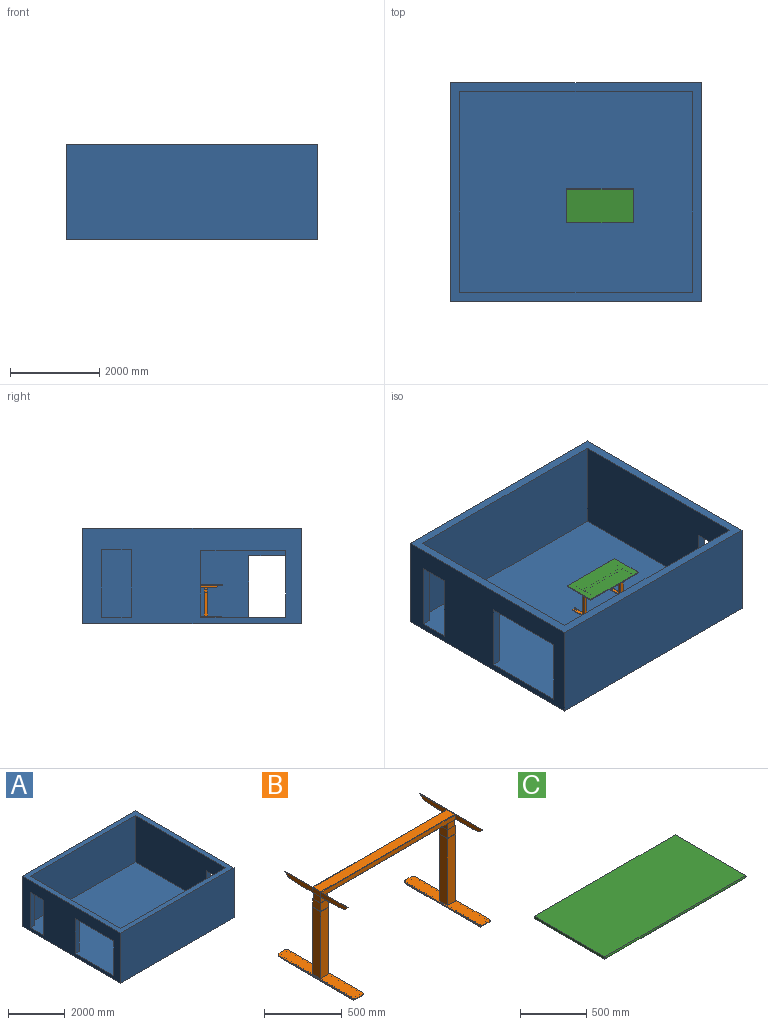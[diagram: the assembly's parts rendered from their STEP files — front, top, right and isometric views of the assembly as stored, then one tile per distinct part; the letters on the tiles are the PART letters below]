
ASSEMBLY  parts=3 mates=2
PART A: 20 faces, bbox 5620x4900x2150 mm
  f0: plane 4500x2000mm, normal (1,0,0), area 5140709mm2, adj f4,f5,f9,f10,f14,f15,f16,f17
  f1: plane 4900x2150mm, normal (-1,0,0), area 6675709mm2, adj f3,f7,f8,f9,f10,f14,f15,f16
  f2: plane 4900x2150mm, normal (1,0,0), area 9320170mm2, adj f3,f7,f8,f9,f10,f11,f12,f13
  f3: plane 5620x4900mm, normal (0,0,-1), area 27538000mm2, adj f1,f2,f7,f8
  f4: plane 5220x2000mm, normal (0,-1,0), area 10440000mm2, adj f0,f6,f9,f10
  f5: plane 5220x2000mm, normal (0,1,0), area 10440000mm2, adj f0,f6,f9,f10
  f6: plane 4500x2000mm, normal (-1,0,0), area 7785170mm2, adj f4,f5,f9,f10,f11,f12,f13
  f7: plane 5620x2150mm, normal (0,1,0), area 12083000mm2, adj f1,f2,f3,f9
  f8: plane 5620x2150mm, normal (0,-1,0), area 12083000mm2, adj f1,f2,f3,f9
  f9: plane 5620x4900mm, normal (0,0,1), area 4048000mm2, adj f0,f1,f2,f4,f5,f6,f7,f8
  f10: plane 5620x4500mm, normal (0,0,1), area 24180418.5mm2, adj f0,f1,f2,f4,f5,f6,f12,f13
  f11: plane 881.69x200mm, normal (0,0,-1), area 176338.6mm2, adj f2,f6,f12,f13
  f12: plane 1377.84x200mm, normal (0,1,0), area 275567.5mm2, adj f2,f6,f10,f11
  f13: plane 1377.84x200mm, normal (0,-1,0), area 275567.5mm2, adj f2,f6,f10,f11
  f14: plane 1496.51x200mm, normal (0,1,0), area 299302.3mm2, adj f0,f1,f10,f15
  f15: plane 1903.46x200mm, normal (0,0,-1), area 380691.5mm2, adj f0,f1,f14,f16
  f16: plane 1496.51x200mm, normal (0,-1,0), area 299302.3mm2, adj f0,f1,f10,f15
  f17: plane 1515.49x200mm, normal (0,-1,0), area 303098.4mm2, adj f0,f1,f10,f19
  f18: plane 1515.49x200mm, normal (0,1,0), area 303098.4mm2, adj f0,f1,f10,f19
  f19: plane 666.94x200mm, normal (0,0,-1), area 133388.4mm2, adj f0,f1,f17,f18
PART B: 100 faces, bbox 1240x707x708 mm
  f0: cylinder r=2.5mm len=72mm, axis (0,1,0), area 266mm2, adj f40,f79,f80,f81,f85,f86,f97,f98
  f1: cylinder r=2.5mm len=72mm, axis (0,1,0), area 266mm2, adj f31,f32,f33,f40,f42,f43,f92,f93
  f2: plane 70x70mm, normal (0,0,1), area 675mm2, adj f27,f28,f29,f30,f31,f32,f33,f34
  f3: plane 75x75mm, normal (0,0,1), area 725mm2, adj f23,f24,f25,f26,f27,f28,f29,f30
  f4: plane 706.96x90mm, normal (0,0,1), area 57657.7mm2, adj f5,f6,f7,f8,f9,f20,f21,f22
  f5: plane 666.96x5mm, normal (-1,0,0), area 3334.8mm2, adj f4,f6,f10,f20
  f6: cylinder r=20mm len=20mm, axis (0,0,-1), area 157.1mm2, adj f4,f5,f7,f10
  f7: plane 50x5mm, normal (0,-1,0), area 250mm2, adj f4,f6,f8,f10
  f8: cylinder r=20mm len=20mm, axis (0,0,-1), area 157.1mm2, adj f4,f7,f9,f10
  f9: plane 666.96x5mm, normal (1,0,0), area 3334.8mm2, adj f4,f8,f10,f22
  f10: plane 706.96x90mm, normal (0,0,-1), area 18161.8mm2, adj f5,f6,f7,f8,f9,f11,f12,f13
  f11: plane 668.86x18mm, normal (1,0,0), area 12039.4mm2, adj f10,f12,f14,f19
  f12: plane 67.46x18mm, normal (0,-1,0), area 1214.3mm2, adj f10,f11,f13,f14
  f13: plane 668.86x18mm, normal (-1,0,0), area 12039.4mm2, adj f10,f12,f14,f19
  f14: plane 668.86x67.46mm, normal (0,0,-1), area 41042.3mm2, adj f11,f12,f13,f15,f18,f19
  f15: cylinder r=25.48mm len=50.96mm, axis (0,0,1), area 800.4mm2, adj f14,f16
  f16: plane 50.96x50.96mm, normal (0,0,-1), area 2039.3mm2, adj f15
  f17: plane 50.96x50.96mm, normal (0,0,-1), area 2039.3mm2, adj f18
  f18: cylinder r=25.48mm len=50.96mm, axis (0,0,1), area 800.4mm2, adj f14,f17
  f19: plane 67.46x18mm, normal (0,1,0), area 1214.3mm2, adj f10,f11,f13,f14
  f20: cylinder r=20mm len=20mm, axis (0,0,-1), area 157.1mm2, adj f4,f5,f10,f21
  f21: plane 50x5mm, normal (0,1,0), area 250mm2, adj f4,f10,f20,f22
  f22: cylinder r=20mm len=20mm, axis (0,0,-1), area 157.1mm2, adj f4,f9,f10,f21
  f23: plane 525x75mm, normal (0,-1,0), area 39375mm2, adj f3,f4,f24,f26
  f24: plane 525x75mm, normal (1,0,0), area 39375mm2, adj f3,f4,f23,f25
  f25: plane 525x75mm, normal (0,1,0), area 39375mm2, adj f3,f4,f24,f26
  f26: plane 525x75mm, normal (-1,0,0), area 39375mm2, adj f3,f4,f23,f25
  f27: plane 70x65mm, normal (0,-1,0), area 4550mm2, adj f2,f3,f28,f30
  f28: plane 70x65mm, normal (1,0,0), area 4550mm2, adj f2,f3,f27,f29
  f29: plane 70x65mm, normal (0,1,0), area 4550mm2, adj f2,f3,f28,f30
  f30: plane 70x65mm, normal (-1,0,0), area 4550mm2, adj f2,f3,f27,f29
  f31: plane 65x50.01mm, normal (0,-1,0), area 3250mm2, adj f1,f2,f32,f34,f40
  f32: plane 65x50.01mm, normal (1,0,0), area 3250.5mm2, adj f1,f2,f31,f33
  f33: plane 65x50.01mm, normal (0,1,0), area 3250mm2, adj f1,f2,f32,f34,f40
  f34: plane 65x50mm, normal (-1,0,0), area 3250mm2, adj f2,f31,f33,f40
  f35: plane 1214.62x35mm, normal (0,-1,0), area 42511.8mm2, adj f36,f41,f45,f83
  f36: cylinder r=2.5mm len=35mm, axis (0,0,-1), area 137.4mm2, adj f35,f42,f46,f90
  f37: cylinder r=2.5mm len=35mm, axis (0,0,-1), area 137.4mm2, adj f38,f43,f48,f90
  f38: plane 1214.62x35mm, normal (0,1,0), area 42511.8mm2, adj f37,f44,f49,f84
  f39: plane 1214.62x72mm, normal (0,0,1), area 87452.2mm2, adj f45,f47,f49,f88
  f40: plane 1214.62x72mm, normal (0,0,-1), area 79026.7mm2, adj f0,f1,f31,f33,f34,f41,f44,f79
  f41: cylinder r=2.5mm len=1214.62mm, axis (1,0,0), area 4769.8mm2, adj f35,f40,f42,f85
  f42: sphere r=2.5mm, area 9.8mm2, adj f1,f36,f41,f90
  f43: sphere r=2.5mm, area 9.8mm2, adj f1,f37,f44,f90
  f44: cylinder r=2.5mm len=1214.62mm, axis (-1,0,0), area 4769.8mm2, adj f38,f40,f43,f86
  f45: cylinder r=2.5mm len=1214.62mm, axis (-1,0,0), area 4769.8mm2, adj f35,f39,f46,f87
  f46: sphere r=2.5mm, area 9.8mm2, adj f36,f45,f47
  f47: cylinder r=2.5mm len=72mm, axis (0,-1,0), area 282.7mm2, adj f39,f46,f48,f90
  f48: sphere r=2.5mm, area 6.2mm2, adj f37,f47,f49
  f49: cylinder r=2.5mm len=1214.62mm, axis (1,0,0), area 4769.8mm2, adj f38,f39,f48,f89
  f50: plane 70x70mm, normal (0,0,1), area 675mm2, adj f75,f76,f77,f78,f79,f80,f81,f82
  f51: plane 75x75mm, normal (0,0,1), area 725mm2, adj f71,f72,f73,f74,f75,f76,f77,f78
  f52: plane 706.96x90mm, normal (0,0,1), area 57657.7mm2, adj f53,f54,f55,f56,f57,f68,f69,f70
  f53: plane 666.96x5mm, normal (1,0,0), area 3334.8mm2, adj f52,f54,f58,f68
  f54: cylinder r=20mm len=20mm, axis (0,0,-1), area 157.1mm2, adj f52,f53,f55,f58
  f55: plane 50x5mm, normal (0,-1,0), area 250mm2, adj f52,f54,f56,f58
  f56: cylinder r=20mm len=20mm, axis (0,0,-1), area 157.1mm2, adj f52,f55,f57,f58
  f57: plane 666.96x5mm, normal (-1,0,0), area 3334.8mm2, adj f52,f56,f58,f70
  f58: plane 706.96x90mm, normal (0,0,-1), area 18161.8mm2, adj f53,f54,f55,f56,f57,f59,f60,f61
  f59: plane 668.86x18mm, normal (-1,0,0), area 12039.4mm2, adj f58,f60,f62,f67
  f60: plane 67.46x18mm, normal (0,-1,0), area 1214.3mm2, adj f58,f59,f61,f62
  f61: plane 668.86x18mm, normal (1,0,0), area 12039.4mm2, adj f58,f60,f62,f67
  f62: plane 668.86x67.46mm, normal (0,0,-1), area 41042.3mm2, adj f59,f60,f61,f63,f66,f67
  f63: cylinder r=25.48mm len=50.96mm, axis (0,0,1), area 800.4mm2, adj f62,f64
  f64: plane 50.96x50.96mm, normal (0,0,-1), area 2039.3mm2, adj f63
  f65: plane 50.96x50.96mm, normal (0,0,-1), area 2039.3mm2, adj f66
  f66: cylinder r=25.48mm len=50.96mm, axis (0,0,1), area 800.4mm2, adj f62,f65
  f67: plane 67.46x18mm, normal (0,1,0), area 1214.3mm2, adj f58,f59,f61,f62
  f68: cylinder r=20mm len=20mm, axis (0,0,-1), area 157.1mm2, adj f52,f53,f58,f69
  f69: plane 50x5mm, normal (0,1,0), area 250mm2, adj f52,f58,f68,f70
  f70: cylinder r=20mm len=20mm, axis (0,0,-1), area 157.1mm2, adj f52,f57,f58,f69
  f71: plane 525x75mm, normal (0,-1,0), area 39375mm2, adj f51,f52,f72,f74
  f72: plane 525x75mm, normal (-1,0,0), area 39375mm2, adj f51,f52,f71,f73
  f73: plane 525x75mm, normal (0,1,0), area 39375mm2, adj f51,f52,f72,f74
  f74: plane 525x75mm, normal (1,0,0), area 39375mm2, adj f51,f52,f71,f73
  f75: plane 70x65mm, normal (0,-1,0), area 4550mm2, adj f50,f51,f76,f78
  f76: plane 70x65mm, normal (-1,0,0), area 4550mm2, adj f50,f51,f75,f77
  f77: plane 70x65mm, normal (0,1,0), area 4550mm2, adj f50,f51,f76,f78
  f78: plane 70x65mm, normal (1,0,0), area 4550mm2, adj f50,f51,f75,f77
  f79: plane 65x50.01mm, normal (0,-1,0), area 3250mm2, adj f0,f40,f50,f80,f82
  f80: plane 65x50.01mm, normal (-1,0,0), area 3250.5mm2, adj f0,f50,f79,f81
  f81: plane 65x50.01mm, normal (0,1,0), area 3250mm2, adj f0,f40,f50,f80,f82
  f82: plane 65x50mm, normal (1,0,0), area 3250mm2, adj f40,f50,f79,f81
  f83: cylinder r=2.5mm len=35mm, axis (0,0,-1), area 137.4mm2, adj f35,f85,f87,f95
  f84: cylinder r=2.5mm len=35mm, axis (0,0,-1), area 137.4mm2, adj f38,f86,f89,f95
  f85: sphere r=2.5mm, area 9.8mm2, adj f0,f41,f83,f95
  f86: sphere r=2.5mm, area 9.8mm2, adj f0,f44,f84,f95
  f87: sphere r=2.5mm, area 6.2mm2, adj f45,f83,f88
  f88: cylinder r=2.5mm len=72mm, axis (0,-1,0), area 282.7mm2, adj f39,f87,f89,f95
  f89: sphere r=2.5mm, area 9.8mm2, adj f49,f84,f88
  f90: plane 570.11x37.77mm, normal (-1,0,0), area 17002mm2, adj f36,f37,f42,f43,f47,f91,f92,f93
  f91: plane 570.1x3mm, normal (0,0,1), area 1710.3mm2, adj f90,f92,f93,f94
  f92: extruded ~285.05x37.73mm, area 889.6mm2, adj f1,f90,f91,f93,f94
  f93: extruded ~285.05x37.73mm, area 890.5mm2, adj f1,f90,f91,f92,f94
  f94: plane 570.1x38.35mm, normal (1,0,0), area 19457.1mm2, adj f91,f92,f93
  f95: plane 570.11x37.77mm, normal (1,0,0), area 17001.3mm2, adj f83,f84,f85,f86,f88,f96,f97,f98
  f96: plane 570.1x3mm, normal (0,0,1), area 1710.3mm2, adj f95,f97,f98,f99
  f97: extruded ~285.05x37.73mm, area 890.5mm2, adj f0,f95,f96,f98,f99
  f98: extruded ~285.05x37.73mm, area 889.6mm2, adj f0,f95,f96,f97,f99
  f99: plane 570.1x38.35mm, normal (-1,0,0), area 19457.1mm2, adj f96,f97,f98
PART C: 6 faces, bbox 1500x756x21 mm
  f0: plane 756x21mm, normal (1,0,0), area 15835.4mm2, adj f2,f3,f4,f5
  f1: plane 756x21mm, normal (-1,0,0), area 15835.4mm2, adj f2,f3,f4,f5
  f2: plane 1500x750mm, normal (0,0,1), area 1125000mm2, adj f0,f1,f4,f5
  f3: plane 1500x750mm, normal (0,0,-1), area 1125000mm2, adj f0,f1,f4,f5
  f4: cylinder r=19.88mm len=1500mm, axis (1,0,0), area 33187.2mm2, adj f0,f1,f2,f3
  f5: cylinder r=19.88mm len=1500mm, axis (1,0,0), area 33187.2mm2, adj f0,f1,f2,f3
PLACE A t=(1120,-1412.67,2630)mm
PLACE B t=(1657.46,-1722.6,2803)mm
PLACE C t=(1657.46,-1721.62,3488)mm
MATE fastened A.f10 <-> B.f66  axis (0,0,1) through (1082.46,-1433.94,2780)mm
MATE fastened C.f3 <-> B.f39  axis (0,0,-1) through (1657.46,-1721.62,3488)mm
